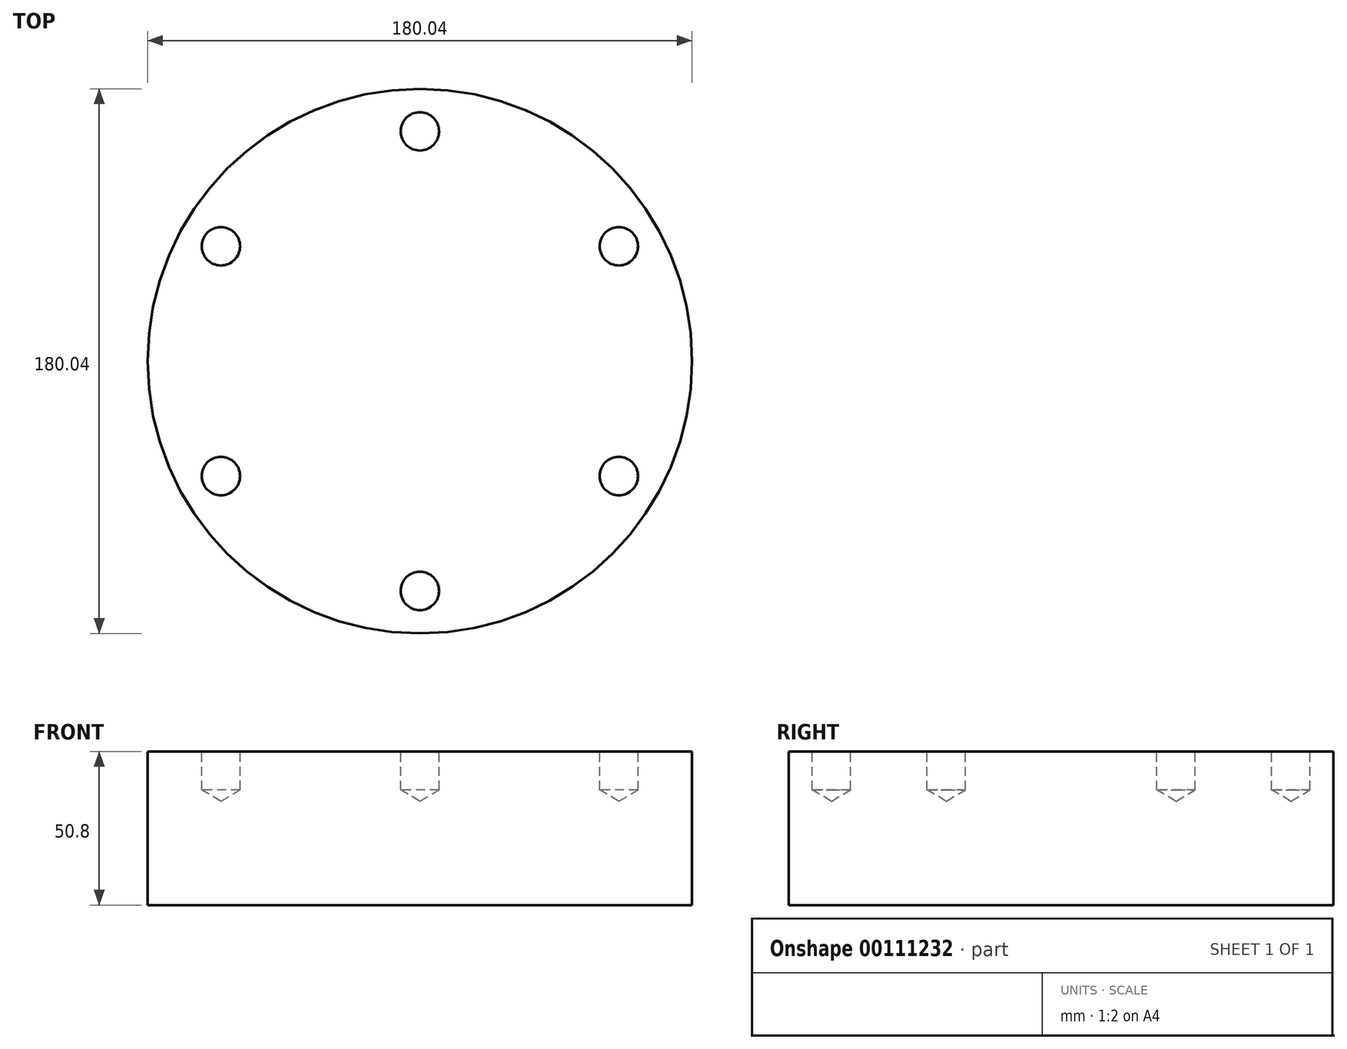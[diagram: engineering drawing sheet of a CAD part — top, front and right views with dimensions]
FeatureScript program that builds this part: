
annotation { "Feature Type Name" : "Feature", "Feature Type Description" : "" }
export const myFeature = defineFeature(function(context is Context, id is Id, definition is map)
    precondition{}
    {
        {
            var Q0;
            Q0=qCreatedBy(makeId("Top.planeOp"),FACE);
            var sketch = newSketch(context, id + "F0", { "sketchPlane" : qUnion([Q0])});
            skCircle(sketch, "E0", {"center": v(0, 0) * mm, "radius": 90.02 * mm});
            skSolve(sketch);
        }
        {
            var Q0;
            Q0=makeQuery(id+"F0.imprint","IMPRINT",FACE,{"disambiguationData":[TD([[makeQuery(id+"F0.imprint","IMPRINT",EDGE,{"derivedFrom":sQuery(id+"F0.wireOp",EDGE,"E0")}),1.0]])]});
            extrude(context, id + "F1", {"entities" : qUnion([Q0]), "endBound" : BoundingType.SYMMETRIC, "depth" : 50.8 * mm});
        }
        {
            var Q0;
            Q0=makeQuery(id+"F1.opExtrude","CAP_FACE",FACE,{"disambiguationData":[OSD([sQuery(id+"F0.wireOp",EDGE,"E0")])],"isStart":false});
            var sketch = newSketch(context, id + "F2", { "sketchPlane" : qUnion([Q0])});
            skPoint(sketch, "E1", {"position": v(0, 75.97) * mm});
            skPoint(sketch, "E2.1.0", {"position": v(-65.8, 37.98) * mm});
            skPoint(sketch, "E2.2.0", {"position": v(-65.8, -37.98) * mm});
            skPoint(sketch, "E2.3.0", {"position": v(0, -75.97) * mm});
            skPoint(sketch, "E2.4.0", {"position": v(65.8, -37.98) * mm});
            skPoint(sketch, "E2.5.0", {"position": v(65.8, 37.98) * mm});
            skPoint(sketch, "E2.center", {"position": v(0, 0) * mm});
            skSolve(sketch);
        }
        {
            var Q0;
            Q0=sQuery(id+"F2.wireOp",VERTEX,"E1");
            var Q1;
            Q1=sQuery(id+"F2.wireOp",VERTEX,"E2.1.0");
            var Q2;
            Q2=sQuery(id+"F2.wireOp",VERTEX,"E2.2.0");
            var Q3;
            Q3=sQuery(id+"F2.wireOp",VERTEX,"E2.3.0");
            var Q4;
            Q4=sQuery(id+"F2.wireOp",VERTEX,"E2.4.0");
            var Q5;
            Q5=sQuery(id+"F2.wireOp",VERTEX,"E2.5.0");
            var Q6;
            Q6=makeQuery(id+"F1.opExtrude","SWEPT_BODY",BODY,{"disambiguationData":[OSD([sQuery(id+"F0.wireOp",EDGE,"E0")])]});
            hole(context, id + "F3", {"style" : HoleStyle.C_BORE, "endStyle" : HoleEndStyle.BLIND, "holeDiameter" : 12.7 * mm, "cBoreDiameter" : 12.7 * mm, "cBoreDepth" : 10.16 * mm, "holeDepth" : 12.7 * mm, "locations" : qUnion([Q0, Q1, Q2, Q3, Q4, Q5]), "scope" : qUnion([Q6])});
        }
    });
